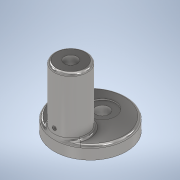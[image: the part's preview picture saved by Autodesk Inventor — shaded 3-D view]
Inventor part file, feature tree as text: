
AUTODESK INVENTOR PART (.ipt)
format: ipt  version: 2020 (Build 240168000, 168)  size: 811,520 bytes
history: native  units: in
note: dims shown in document units (in); Inventor stores cm internally (conversion verified against a paired STEP export)
features: sketch x6, extrude x5, fillet x2, plane x1, hole x1, thread x1, revolve x1, helix x1
ambient origin geometry x8: Origin, YZ Plane, XZ Plane, XY Plane, X Axis, Y Axis, Z Axis, Center Point
bodies: Solid1 (feature_tree), Solid2 (feature_tree)
feature tree (18):
  extrude  "Extrusion1"  Depth=0.625in TaperAngle=0.0deg
  sketch  "Sketch2"  dims[d3=1.625in d5=0.6562in]
  extrude  "Extrusion2"  Depth=0.6562in
  extrude  "Extrusion3"  Depth=1.2813in
  extrude  "Extrusion4"  TaperAngle=0.0deg  [1 undecoded]
  extrude  "Extrusion5"  Depth=0.626in
  fillet  "Fillet1"  [1 undecoded]
  plane  "Work Plane1"
  hole  "Hole1"  [1 undecoded]
  thread  "Thread1"  [1 undecoded]
  revolve  "Revolution1"  [1 undecoded]
  helix  "Coil1"  [1 undecoded]
  fillet  "Fillet2"  Radius=0.3779in
  sketch  "Sketch1"  dims[d0=3.5625in d1=0.625in d2=0.0in]
  sketch  "Sketch3"  dims[d6=1.5625in d7=1.2813in]
  sketch  "Sketch4"  dims[d8=2.875in d9=0.0in d10=0.0in d11=0.0in]
  sketch  "Sketch5"  dims[d12=0.0625in d13=0.0in d14=0.626in d15=0.0in d16=0.0in]
  sketch  "Sketch6"  dims[d17=0.125in d18=1.0in d19=0.196in d20=0.5in d21=0.375in d22=0.25in d23=0.5635in d24=0.75in d25=0.0in d26=0.515in d27=0.0in d28=0.3779in d29=0.008in d30=0.008in d33=0.05in d35=0.3779in d37=0.0in d38=0.05in d39=0.6152in d40=0.3937in d41=0.0in d42=0.0in d43=0.0in d44=0.0in d45=0.0in d46=0.125in]
note: 6 required parameter values undecoded (feature->parameter linkage not recoverable at this tier; creation-order binding heuristic only, values carry confidence <= 0.55)